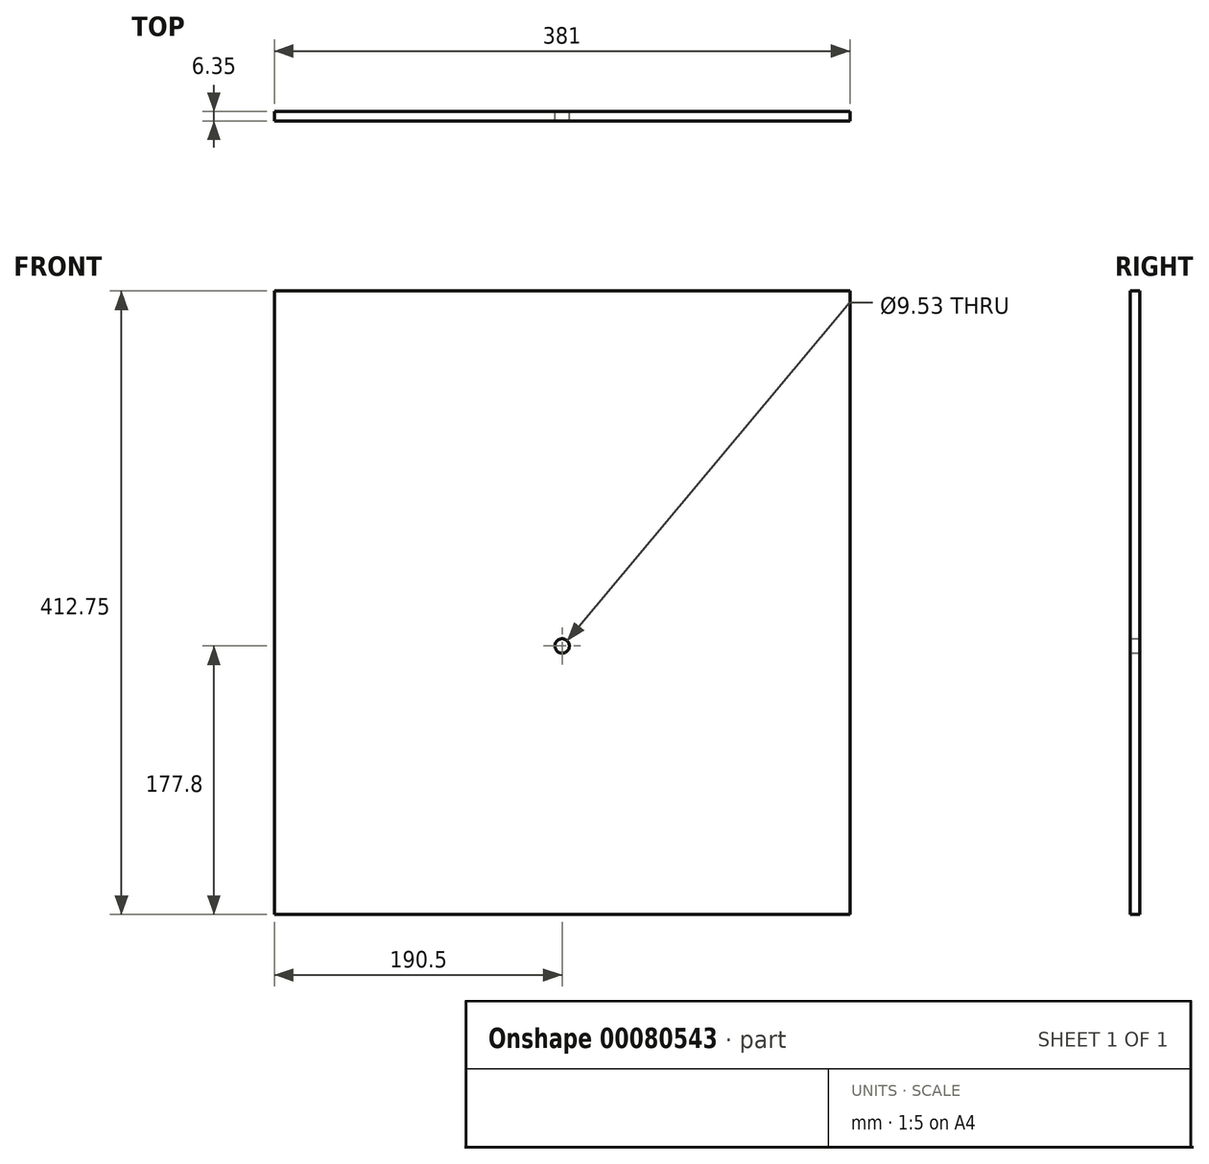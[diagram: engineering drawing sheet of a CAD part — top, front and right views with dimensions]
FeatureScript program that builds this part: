
annotation { "Feature Type Name" : "Feature", "Feature Type Description" : "" }
export const myFeature = defineFeature(function(context is Context, id is Id, definition is map)
    precondition{}
    {
        {
            var Q0;
            Q0=qCreatedBy(makeId("Front.planeOp"),FACE);
            var sketch = newSketch(context, id + "F0", { "sketchPlane" : qUnion([Q0])});
            skLineSegment(sketch, "E0.bottom", {"start": v(-190.5, 234.95) * mm, "end": v(190.5, 234.95) * mm});
            skLineSegment(sketch, "E0.top", {"start": v(-190.5, -177.8) * mm, "end": v(190.5, -177.8) * mm});
            skLineSegment(sketch, "E0.left", {"start": v(-190.5, 234.95) * mm, "end": v(-190.5, -177.8) * mm});
            skLineSegment(sketch, "E0.right", {"start": v(190.5, 234.95) * mm, "end": v(190.5, -177.8) * mm});
            skCircle(sketch, "E1", {"center": v(0, 0) * mm, "radius": 4.76 * mm});
            skSolve(sketch);
        }
        {
            var Q0;
            Q0=makeQuery(id+"F0.imprint","IMPRINT",FACE,{"disambiguationData":[TD([[makeQuery(id+"F0.imprint","IMPRINT",EDGE,{"derivedFrom":sQuery(id+"F0.wireOp",EDGE,"E0.bottom")}),-1.0]])]});
            extrude(context, id + "F1", {"entities" : qUnion([Q0]), "depth" : 6.35 * mm});
        }
    });
